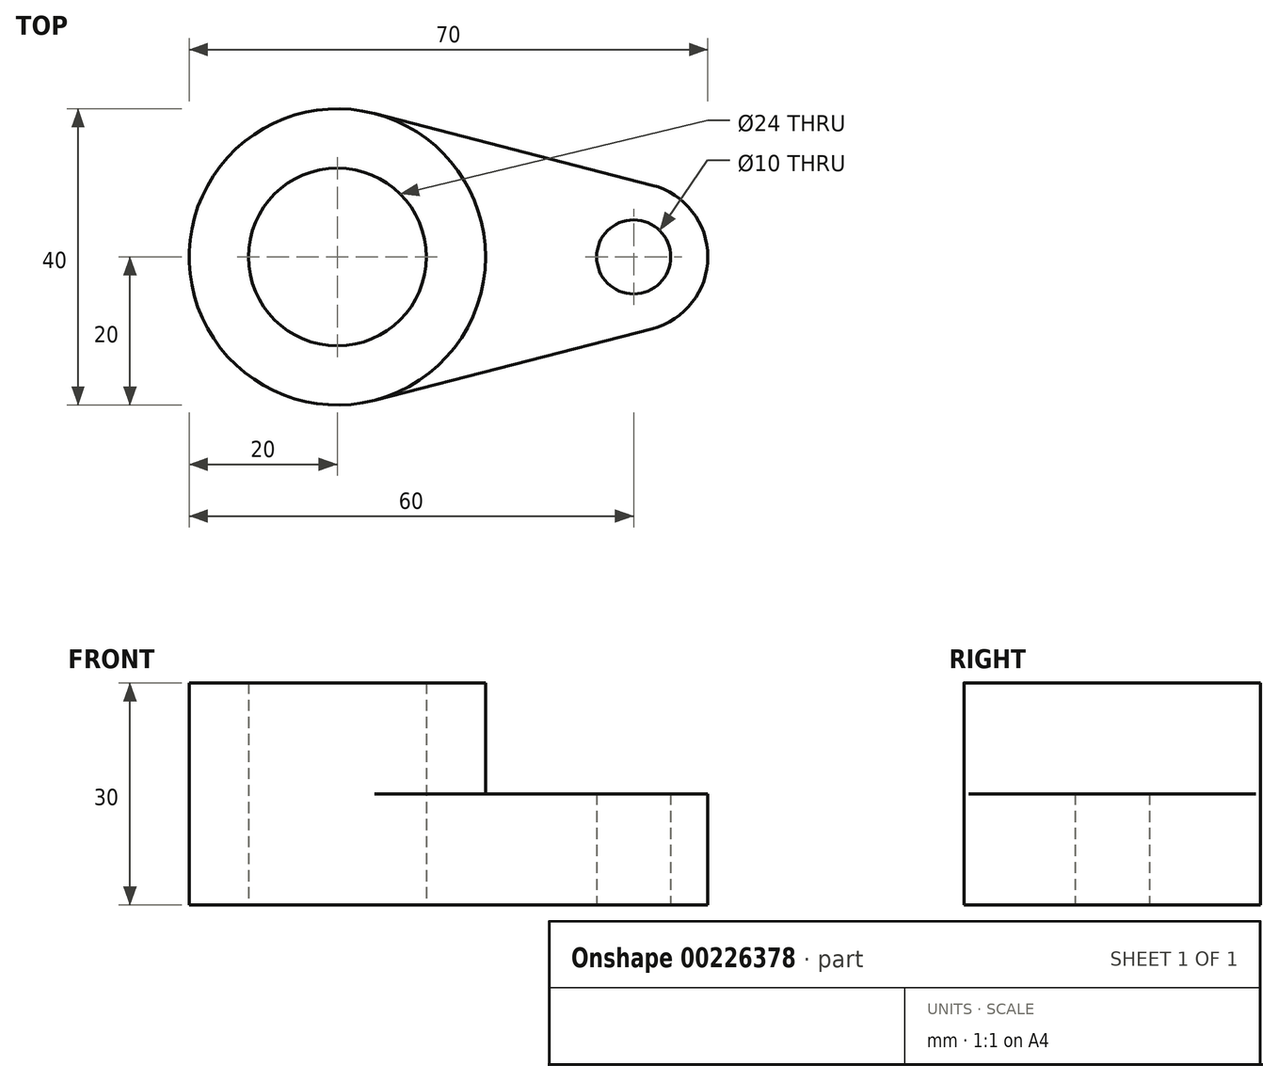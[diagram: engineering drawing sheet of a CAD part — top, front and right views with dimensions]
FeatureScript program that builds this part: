
annotation { "Feature Type Name" : "Feature", "Feature Type Description" : "" }
export const myFeature = defineFeature(function(context is Context, id is Id, definition is map)
    precondition{}
    {
        {
            var Q0;
            Q0=qCreatedBy(makeId("Top.planeOp"),FACE);
            var sketch = newSketch(context, id + "F0", { "sketchPlane" : qUnion([Q0])});
            skArc(sketch, "E0", {"start": v(5, 19.36) * mm, "mid": v(-20, 0) * mm, "end": v(5, -19.36) * mm});
            skArc(sketch, "E1", {"start": v(42.5, -9.68) * mm, "mid": v(50, 0) * mm, "end": v(42.5, 9.68) * mm});
            skLineSegment(sketch, "E2", {"start": v(5, 19.36) * mm, "end": v(42.5, 9.68) * mm});
            skLineSegment(sketch, "E3", {"start": v(5, -19.36) * mm, "end": v(42.5, -9.68) * mm});
            skCircle(sketch, "E4", {"center": v(0, 0) * mm, "radius": 12 * mm});
            skCircle(sketch, "E5", {"center": v(40, 0) * mm, "radius": 5 * mm});
            skSolve(sketch);
        }
        {
            var Q0;
            Q0=makeQuery(id+"F0.imprint","IMPRINT",FACE,{"disambiguationData":[TD([[makeQuery(id+"F0.imprint","IMPRINT",EDGE,{"derivedFrom":sQuery(id+"F0.wireOp",EDGE,"E0")}),1.0]])]});
            extrude(context, id + "F1", {"entities" : qUnion([Q0]), "depth" : 15 * mm});
        }
        {
            var Q0;
            Q0=makeQuery(id+"F1.opExtrude","CAP_FACE",FACE,{"disambiguationData":[OSD([sQuery(id+"F0.wireOp",EDGE,"E0"),sQuery(id+"F0.wireOp",EDGE,"E1"),sQuery(id+"F0.wireOp",EDGE,"E2"),sQuery(id+"F0.wireOp",EDGE,"E3"),sQuery(id+"F0.wireOp",EDGE,"E4"),sQuery(id+"F0.wireOp",EDGE,"E5")])],"isStart":false});
            var sketch = newSketch(context, id + "F2", { "sketchPlane" : qUnion([Q0])});
            skCircle(sketch, "E6", {"center": v(0, 0) * mm, "radius": 20 * mm});
            skSolve(sketch);
        }
        {
            var Q0;
            Q0=makeQuery(id+"F2.imprint","IMPRINT",FACE,{"disambiguationData":[TD([[makeQuery(id+"F2.imprint","IMPRINT",EDGE,{"derivedFrom":makeQuery(id+"F1.opExtrude","CAP_EDGE",EDGE,{"disambiguationData":[OSD([sQuery(id+"F0.wireOp",EDGE,"E4")])],"isStart":false})}),-1.0]])]});
            extrude(context, id + "F3", {"entities" : qUnion([Q0]), "operationType" : NewBodyOperationType.ADD, "depth" : 15 * mm});
        }
    });
